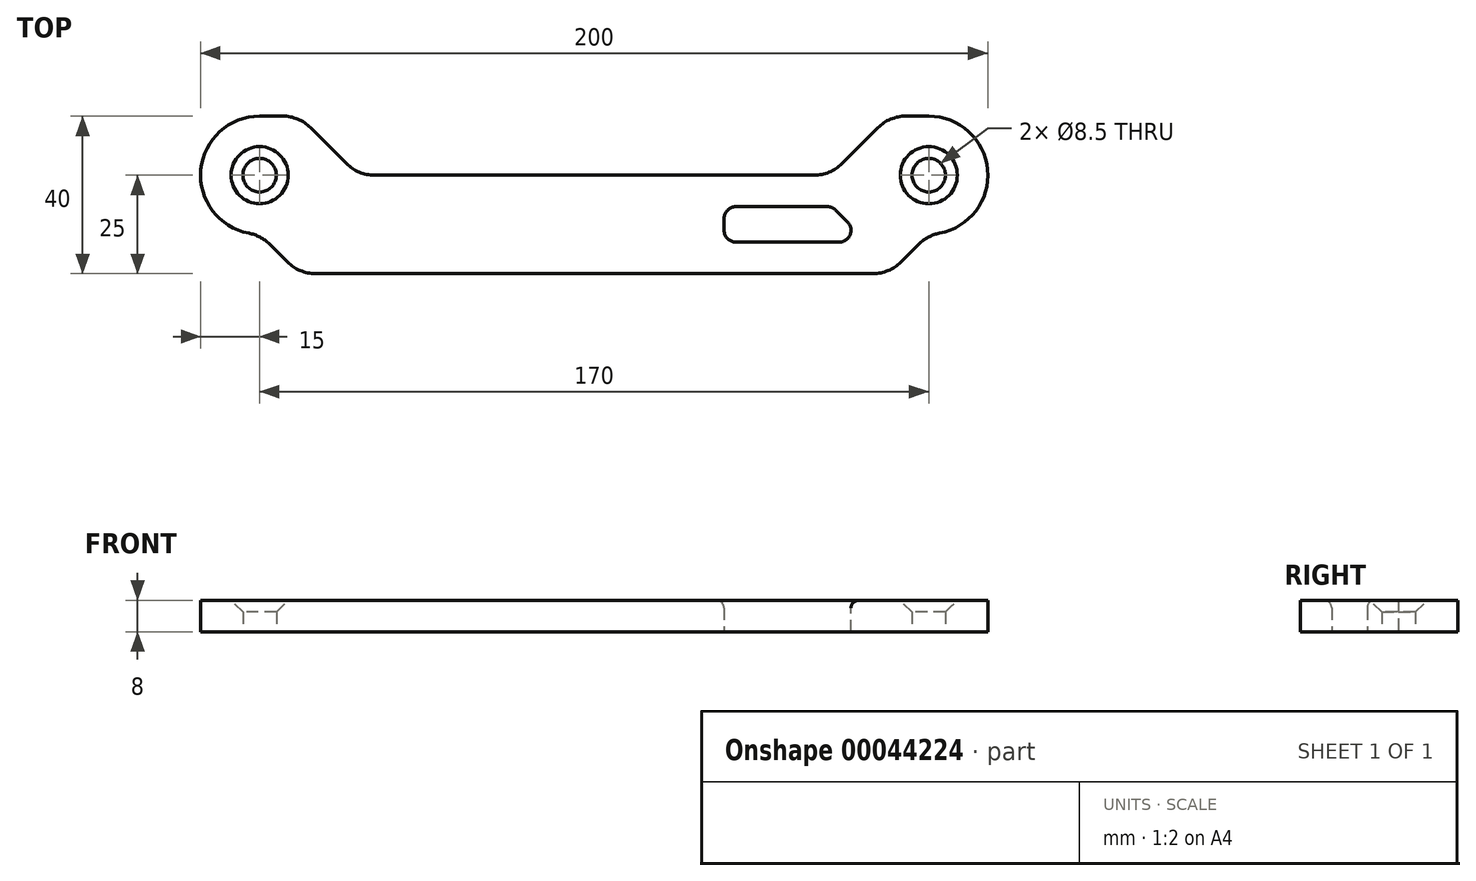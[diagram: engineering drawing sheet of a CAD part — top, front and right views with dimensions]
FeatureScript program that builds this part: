
annotation { "Feature Type Name" : "Feature", "Feature Type Description" : "" }
export const myFeature = defineFeature(function(context is Context, id is Id, definition is map)
    precondition{}
    {
        {
            var Q0;
            Q0=qCreatedBy(makeId("Top.planeOp"),FACE);
            var sketch = newSketch(context, id + "F0", { "sketchPlane" : qUnion([Q0])});
            skLineSegment(sketch, "E0.bottom", {"start": v(-60, 0) * mm, "end": v(60, 0) * mm});
            skLineSegment(sketch, "E1", {"start": v(75, -25) * mm, "end": v(-75, -25) * mm});
            skLineSegment(sketch, "E2", {"start": v(-75, -25) * mm, "end": v(-85, -15) * mm});
            skLineSegment(sketch, "E3", {"start": v(-60, 0) * mm, "end": v(-75, 15) * mm});
            skLineSegment(sketch, "E4", {"start": v(-75, 15) * mm, "end": v(-85, 15) * mm});
            skArc(sketch, "E5", {"start": v(-85, 15) * mm, "mid": v(-100, 0) * mm, "end": v(-85, -15) * mm});
            skLineSegment(sketch, "E6", {"start": v(60, 0) * mm, "end": v(75, 15) * mm});
            skLineSegment(sketch, "E7", {"start": v(75, 15) * mm, "end": v(85, 15) * mm});
            skLineSegment(sketch, "E8", {"start": v(75, -25) * mm, "end": v(85, -15) * mm});
            skArc(sketch, "E9", {"start": v(85, -15) * mm, "mid": v(100, 0) * mm, "end": v(85, 15) * mm});
            skCircle(sketch, "E10", {"center": v(-85, 0) * mm, "radius": 4.25 * mm});
            skCircle(sketch, "E11", {"center": v(85, 0) * mm, "radius": 4.25 * mm});
            skSolve(sketch);
        }
        {
            var Q0;
            Q0 = qSketchRegion(id + "F0", true);
            extrude(context, id + "F1", {"entities" : qUnion([Q0]), "depth" : 8 * mm});
        }
        {
            var Q0;
            Q0=makeQuery(id+"F1.opExtrude","SWEPT_EDGE",EDGE,{"disambiguationData":[OSD([sQuery(id+"F0.wireOp",EDGE,"E1"),sQuery(id+"F0.wireOp",EDGE,"E2")])]});
            var Q1;
            Q1=makeQuery(id+"F1.opExtrude","SWEPT_EDGE",EDGE,{"disambiguationData":[OSD([sQuery(id+"F0.wireOp",EDGE,"E2"),sQuery(id+"F0.wireOp",EDGE,"E5")])]});
            var Q2;
            Q2=makeQuery(id+"F1.opExtrude","SWEPT_EDGE",EDGE,{"disambiguationData":[OSD([sQuery(id+"F0.wireOp",EDGE,"E1"),sQuery(id+"F0.wireOp",EDGE,"E8")])]});
            var Q3;
            Q3=makeQuery(id+"F1.opExtrude","SWEPT_EDGE",EDGE,{"disambiguationData":[OSD([sQuery(id+"F0.wireOp",EDGE,"E8"),sQuery(id+"F0.wireOp",EDGE,"E9")])]});
            var Q4;
            Q4=makeQuery(id+"F1.opExtrude","SWEPT_EDGE",EDGE,{"disambiguationData":[OSD([sQuery(id+"F0.wireOp",EDGE,"E3"),sQuery(id+"F0.wireOp",EDGE,"E4")])]});
            var Q5;
            Q5=makeQuery(id+"F1.opExtrude","SWEPT_EDGE",EDGE,{"disambiguationData":[OSD([sQuery(id+"F0.wireOp",EDGE,"E0.bottom"),sQuery(id+"F0.wireOp",EDGE,"E3")])]});
            var Q6;
            Q6=makeQuery(id+"F1.opExtrude","SWEPT_EDGE",EDGE,{"disambiguationData":[OSD([sQuery(id+"F0.wireOp",EDGE,"E0.bottom"),sQuery(id+"F0.wireOp",EDGE,"E6")])]});
            var Q7;
            Q7=makeQuery(id+"F1.opExtrude","SWEPT_EDGE",EDGE,{"disambiguationData":[OSD([sQuery(id+"F0.wireOp",EDGE,"E6"),sQuery(id+"F0.wireOp",EDGE,"E7")])]});
            fillet(context, id + "F2", {"entities" : qUnion([Q0, Q1, Q2, Q3, Q4, Q5, Q6, Q7]), "radius" : 10 * mm, "tangentPropagation" : true, "allowEdgeOverflow" : false});
        }
        {
            var Q0;
            Q0=makeQuery(id+"F1.opExtrude","CAP_EDGE",EDGE,{"disambiguationData":[OSD([sQuery(id+"F0.wireOp",EDGE,"E10")])],"isStart":false});
            var Q1;
            Q1=makeQuery(id+"F1.opExtrude","CAP_EDGE",EDGE,{"disambiguationData":[OSD([sQuery(id+"F0.wireOp",EDGE,"E11")])],"isStart":false});
            chamfer(context, id + "F3", {"entities" : qUnion([Q0, Q1]), "width" : 3 * mm, "tangentPropagation" : true});
        }
        {
            var Q0;
            Q0=qCreatedBy(makeId("Top.planeOp"),FACE);
            var sketch = newSketch(context, id + "F4", { "sketchPlane" : qUnion([Q0])});
            skLineSegment(sketch, "E12", {"start": v(69.47, -17) * mm, "end": v(33, -17) * mm});
            skLineSegment(sketch, "E13", {"start": v(33, -17) * mm, "end": v(33, -8) * mm});
            skLineSegment(sketch, "E14", {"start": v(33, -8) * mm, "end": v(60.47, -8) * mm});
            skLineSegment(sketch, "E15", {"start": v(60.47, -8) * mm, "end": v(69.47, -17) * mm});
            skCircle(sketch, "E16", {"center": v(85, 0) * mm, "radius": 15 * mm, "construction": true});
            skSolve(sketch);
        }
        {
            var Q0;
            Q0 = qSketchRegion(id + "F4", true);
            extrude(context, id + "F5", {"entities" : qUnion([Q0]), "operationType" : NewBodyOperationType.REMOVE, "endBound" : BoundingType.THROUGH_ALL, "depth" : 25 * mm});
        }
        {
            var Q0;
            Q0=makeQuery(id+"F5.boolean.opBoolean","COPY",EDGE,{"derivedFrom":makeQuery(id+"F5.opExtrude","SWEPT_EDGE",EDGE,{"disambiguationData":[OSD([sQuery(id+"F4.wireOp",EDGE,"E14"),sQuery(id+"F4.wireOp",EDGE,"E15")])]})});
            var Q1;
            Q1=makeQuery(id+"F5.boolean.opBoolean","COPY",EDGE,{"derivedFrom":makeQuery(id+"F5.opExtrude","SWEPT_EDGE",EDGE,{"disambiguationData":[OSD([sQuery(id+"F4.wireOp",EDGE,"E13"),sQuery(id+"F4.wireOp",EDGE,"E14")])]})});
            var Q2;
            Q2=makeQuery(id+"F5.boolean.opBoolean","COPY",EDGE,{"derivedFrom":makeQuery(id+"F5.opExtrude","SWEPT_EDGE",EDGE,{"disambiguationData":[OSD([sQuery(id+"F4.wireOp",EDGE,"E12"),sQuery(id+"F4.wireOp",EDGE,"E13")])]})});
            var Q3;
            Q3=makeQuery(id+"F5.boolean.opBoolean","COPY",EDGE,{"derivedFrom":makeQuery(id+"F5.opExtrude","SWEPT_EDGE",EDGE,{"disambiguationData":[OSD([sQuery(id+"F4.wireOp",EDGE,"E12"),sQuery(id+"F4.wireOp",EDGE,"E15")])]})});
            fillet(context, id + "F6", {"entities" : qUnion([Q0, Q1, Q2, Q3]), "radius" : 3 * mm, "tangentPropagation" : true, "allowEdgeOverflow" : false});
        }
        {
            var Q0;
            Q0=makeQuery(id+"F5.boolean.opBoolean","INTERSECT",EDGE,{"derivedFrom":[makeQuery(id+"F1.opExtrude","CAP_FACE",FACE,{"disambiguationData":[OSD([sQuery(id+"F0.wireOp",EDGE,"E0.bottom"),sQuery(id+"F0.wireOp",EDGE,"E1"),sQuery(id+"F0.wireOp",EDGE,"E2"),sQuery(id+"F0.wireOp",EDGE,"E3"),sQuery(id+"F0.wireOp",EDGE,"E4"),sQuery(id+"F0.wireOp",EDGE,"E5"),sQuery(id+"F0.wireOp",EDGE,"E6"),sQuery(id+"F0.wireOp",EDGE,"E7"),sQuery(id+"F0.wireOp",EDGE,"E8"),sQuery(id+"F0.wireOp",EDGE,"E9"),sQuery(id+"F0.wireOp",EDGE,"E10"),sQuery(id+"F0.wireOp",EDGE,"E11")])],"isStart":false}),makeQuery(id+"F5.opExtrude","SWEPT_FACE",FACE,{"disambiguationData":[OSD([sQuery(id+"F4.wireOp",EDGE,"E14")])]})]});
            fillet(context, id + "F7", {"entities" : qUnion([Q0]), "radius" : 2 * mm, "tangentPropagation" : true, "allowEdgeOverflow" : false});
        }
    });
